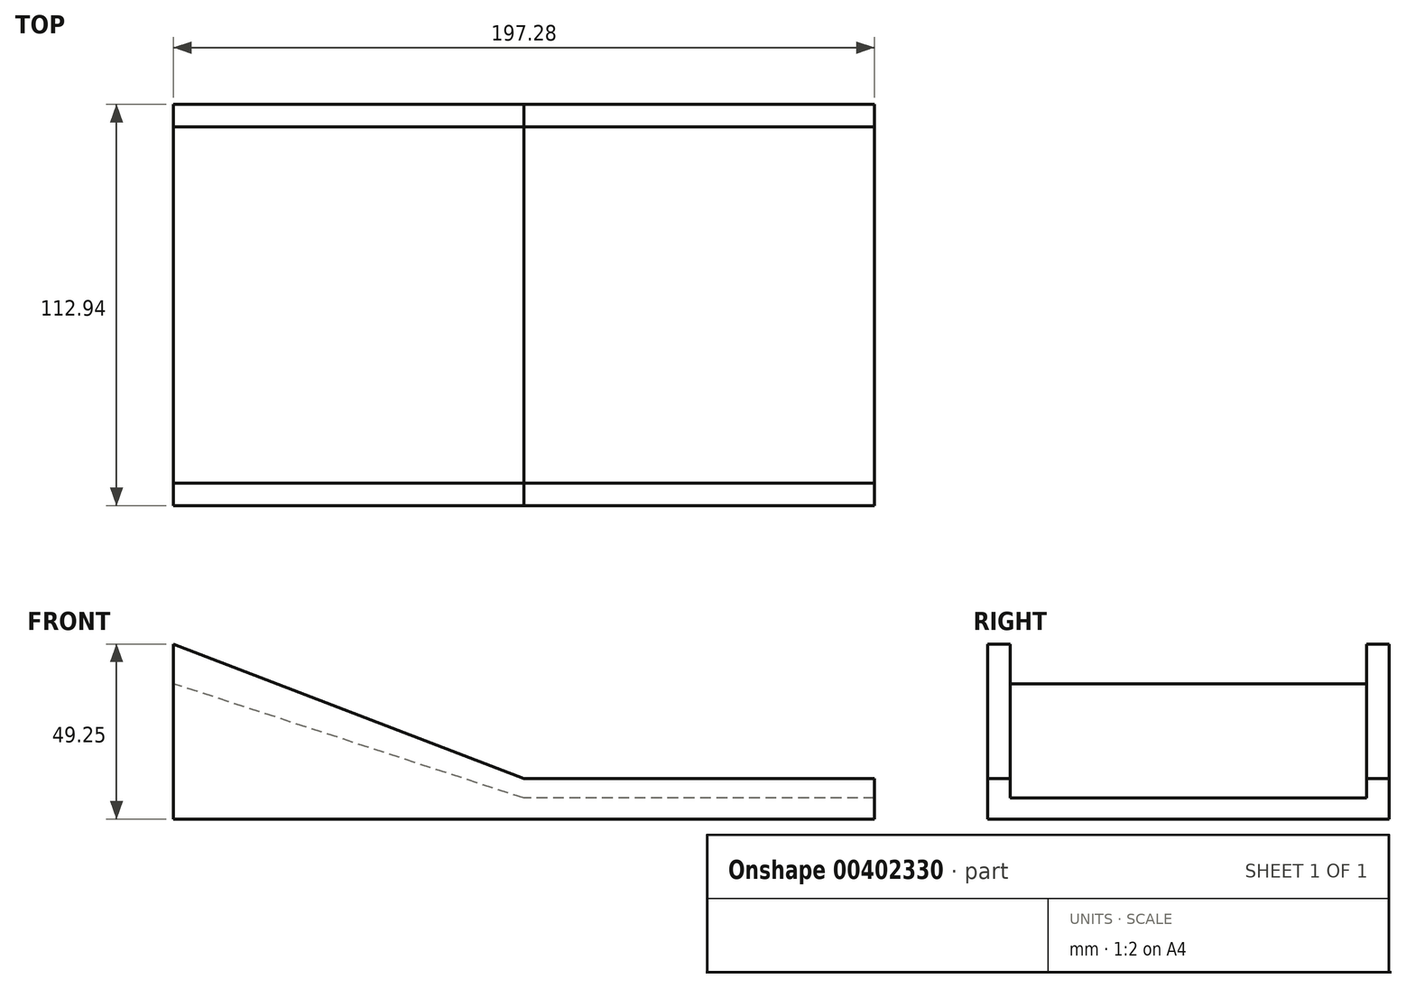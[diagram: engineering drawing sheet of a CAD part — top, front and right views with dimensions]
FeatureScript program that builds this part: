
annotation { "Feature Type Name" : "Feature", "Feature Type Description" : "" }
export const myFeature = defineFeature(function(context is Context, id is Id, definition is map)
    precondition{}
    {
        {
            var Q0;
            Q0=qCreatedBy(makeId("Top.planeOp"),FACE);
            var sketch = newSketch(context, id + "F0", { "sketchPlane" : qUnion([Q0])});
            skLineSegment(sketch, "E0.bottom", {"start": v(-98.64, -50.12) * mm, "end": v(98.64, -50.12) * mm});
            skLineSegment(sketch, "E0.top", {"start": v(-98.64, 50.12) * mm, "end": v(98.64, 50.12) * mm});
            skLineSegment(sketch, "E0.left", {"start": v(-98.64, -50.12) * mm, "end": v(-98.64, 50.12) * mm});
            skLineSegment(sketch, "E0.right", {"start": v(98.64, -50.12) * mm, "end": v(98.64, 50.12) * mm});
            skPoint(sketch, "E0.middle", {"position": v(0, 0) * mm});
            skSolve(sketch);
        }
        {
            var Q0;
            Q0 = qSketchRegion(id + "F0", true);
            extrude(context, id + "F1", {"entities" : qUnion([Q0]), "depth" : 38.1 * mm});
        }
        {
            var Q0;
            Q0=makeQuery(id+"F1.opExtrude","SWEPT_FACE",FACE,{"disambiguationData":[OSD([sQuery(id+"F0.wireOp",EDGE,"E0.bottom")])]});
            var sketch = newSketch(context, id + "F2", { "sketchPlane" : qUnion([Q0])});
            skLineSegment(sketch, "E1", {"start": v(-98.64, 38.1) * mm, "end": v(0, 5.88) * mm});
            skLineSegment(sketch, "E2", {"start": v(0, 5.88) * mm, "end": v(98.64, 5.88) * mm});
            skSolve(sketch);
        }
        {
            var Q0;
            Q0=makeQuery(id+"F2.imprint","IMPRINT",FACE,{"disambiguationData":[TD([[makeQuery(id+"F2.imprint","IMPRINT",EDGE,{"derivedFrom":sQuery(id+"F2.wireOp",EDGE,"E1")}),1.0]])]});
            extrude(context, id + "F3", {"entities" : qUnion([Q0]), "operationType" : NewBodyOperationType.REMOVE, "endBound" : BoundingType.THROUGH_ALL, "oppositeDirection" : true, "depth" : 25.4 * mm});
        }
        {
            var Q0;
            Q0=makeQuery(id+"F1.opExtrude","SWEPT_FACE",FACE,{"disambiguationData":[OSD([sQuery(id+"F0.wireOp",EDGE,"E0.bottom")])]});
            var sketch = newSketch(context, id + "F4", { "sketchPlane" : qUnion([Q0])});
            skLineSegment(sketch, "E3", {"start": v(-98.64, 0) * mm, "end": v(-98.64, 49.25) * mm});
            skLineSegment(sketch, "E4", {"start": v(-98.64, 49.25) * mm, "end": v(0, 11.34) * mm});
            skLineSegment(sketch, "E5", {"start": v(0, 11.34) * mm, "end": v(98.64, 11.34) * mm});
            skPoint(sketch, "E5.endSnap0", {"position": v(98.64, 2.94) * mm});
            skLineSegment(sketch, "E6", {"start": v(98.64, 11.34) * mm, "end": v(98.64, 0) * mm});
            skLineSegment(sketch, "E7", {"start": v(98.64, 0) * mm, "end": v(-98.64, 0) * mm});
            skSolve(sketch);
        }
        {
            var Q0;
            Q0 = qSketchRegion(id + "F4", true);
            extrude(context, id + "F5", {"entities" : qUnion([Q0]), "operationType" : NewBodyOperationType.ADD, "depth" : 6.35 * mm});
        }
        {
            var Q0;
            Q0=makeQuery(id+"F1.opExtrude","SWEPT_FACE",FACE,{"disambiguationData":[OSD([sQuery(id+"F0.wireOp",EDGE,"E0.top")])]});
            var sketch = newSketch(context, id + "F6", { "sketchPlane" : qUnion([Q0])});
            skLineSegment(sketch, "E8", {"start": v(98.64, 0) * mm, "end": v(98.64, 49.25) * mm});
            skLineSegment(sketch, "E9", {"start": v(98.64, 49.25) * mm, "end": v(0, 11.34) * mm});
            skLineSegment(sketch, "E10", {"start": v(0, 11.34) * mm, "end": v(-98.64, 11.34) * mm});
            skLineSegment(sketch, "E11", {"start": v(-98.64, 11.34) * mm, "end": v(-98.64, 0) * mm});
            skLineSegment(sketch, "E12", {"start": v(-98.64, 0) * mm, "end": v(98.64, 0) * mm});
            skSolve(sketch);
        }
        {
            var Q0;
            Q0 = qSketchRegion(id + "F6", true);
            extrude(context, id + "F7", {"entities" : qUnion([Q0]), "operationType" : NewBodyOperationType.ADD, "depth" : 6.35 * mm});
        }
    });
